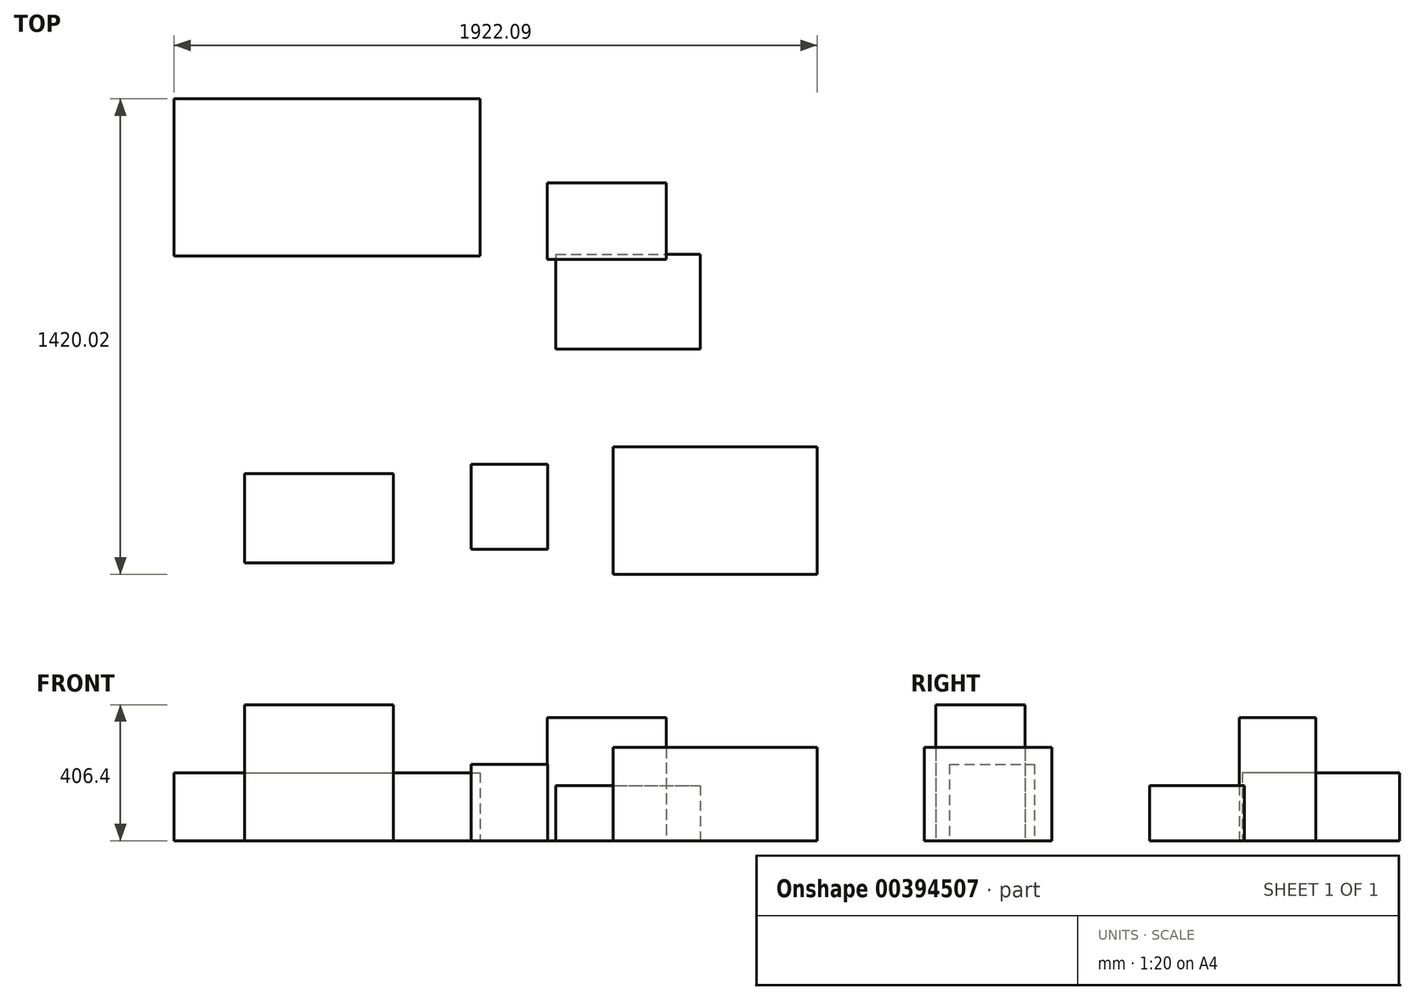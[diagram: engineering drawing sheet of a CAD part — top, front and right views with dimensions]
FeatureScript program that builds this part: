
annotation { "Feature Type Name" : "Feature", "Feature Type Description" : "" }
export const myFeature = defineFeature(function(context is Context, id is Id, definition is map)
    precondition{}
    {
        {
            var Q0;
            Q0=qCreatedBy(makeId("Top.planeOp"),FACE);
            var sketch = newSketch(context, id + "F0", { "sketchPlane" : qUnion([Q0])});
            skLineSegment(sketch, "E0.bottom", {"start": v(-333.22, 250.35) * mm, "end": v(581.18, 250.35) * mm});
            skLineSegment(sketch, "E0.top", {"start": v(-333.22, -219.55) * mm, "end": v(581.18, -219.55) * mm});
            skLineSegment(sketch, "E0.left", {"start": v(-333.22, 250.35) * mm, "end": v(-333.22, -219.55) * mm});
            skLineSegment(sketch, "E0.right", {"start": v(581.18, 250.35) * mm, "end": v(581.18, -219.55) * mm});
            skSolve(sketch);
        }
        {
            var Q0;
            Q0 = qSketchRegion(id + "F0", true);
            extrude(context, id + "F1", {"entities" : qUnion([Q0]), "depth" : 203.2 * mm});
        }
        {
            var Q0;
            Q0=qCreatedBy(makeId("Top.planeOp"),FACE);
            var sketch = newSketch(context, id + "F2", { "sketchPlane" : qUnion([Q0])});
            skLineSegment(sketch, "E1.bottom", {"start": v(782.39, 368.3) * mm, "end": v(1137.99, 368.3) * mm});
            skLineSegment(sketch, "E1.top", {"start": v(782.39, 0) * mm, "end": v(1137.99, 0) * mm});
            skLineSegment(sketch, "E1.left", {"start": v(782.39, 368.3) * mm, "end": v(782.39, 0) * mm});
            skLineSegment(sketch, "E1.right", {"start": v(1137.99, 368.3) * mm, "end": v(1137.99, 0) * mm});
            skSolve(sketch);
        }
        {
            var Q0;
            Q0=makeQuery(id+"F2.imprint","IMPRINT",FACE,{"disambiguationData":[TD([[makeQuery(id+"F2.imprint","IMPRINT",EDGE,{"derivedFrom":sQuery(id+"F2.wireOp",EDGE,"E1.bottom")}),-1.0]])]});
            extrude(context, id + "F3", {"entities" : qUnion([Q0]), "depth" : 228.6 * mm});
        }
        {
            var Q0;
            Q0=qCreatedBy(makeId("Top.planeOp"),FACE);
            var sketch = newSketch(context, id + "F4", { "sketchPlane" : qUnion([Q0])});
            skLineSegment(sketch, "E2.bottom", {"start": v(807.6, -214.07) * mm, "end": v(1239.4, -214.07) * mm});
            skLineSegment(sketch, "E2.top", {"start": v(807.6, -496.64) * mm, "end": v(1239.4, -496.64) * mm});
            skLineSegment(sketch, "E2.left", {"start": v(807.6, -214.07) * mm, "end": v(807.6, -496.64) * mm});
            skLineSegment(sketch, "E2.right", {"start": v(1239.4, -214.07) * mm, "end": v(1239.4, -496.64) * mm});
            skSolve(sketch);
        }
        {
            var Q0;
            Q0=makeQuery(id+"F4.imprint","IMPRINT",FACE,{"disambiguationData":[TD([[makeQuery(id+"F4.imprint","IMPRINT",EDGE,{"derivedFrom":sQuery(id+"F4.wireOp",EDGE,"E2.bottom")}),-1.0]])]});
            extrude(context, id + "F5", {"entities" : qUnion([Q0]), "depth" : 165.1 * mm});
        }
        {
            var Q0;
            Q0=qCreatedBy(makeId("Top.planeOp"),FACE);
            var sketch = newSketch(context, id + "F6", { "sketchPlane" : qUnion([Q0])});
            skLineSegment(sketch, "E3.bottom", {"start": v(-122.07, -462.25) * mm, "end": v(322.43, -462.25) * mm});
            skLineSegment(sketch, "E3.top", {"start": v(-122.07, -868.65) * mm, "end": v(322.43, -868.65) * mm});
            skLineSegment(sketch, "E3.left", {"start": v(-122.07, -462.25) * mm, "end": v(-122.07, -868.65) * mm});
            skLineSegment(sketch, "E3.right", {"start": v(322.43, -462.25) * mm, "end": v(322.43, -868.65) * mm});
            skSolve(sketch);
        }
        {
            var Q0;
            Q0=makeQuery(id+"F6.imprint","IMPRINT",FACE,{"disambiguationData":[TD([[makeQuery(id+"F6.imprint","IMPRINT",EDGE,{"derivedFrom":sQuery(id+"F6.wireOp",EDGE,"E3.bottom")}),-1.0]])]});
            extrude(context, id + "F7", {"entities" : qUnion([Q0]), "depth" : 266.7 * mm});
        }
        {
            var Q0;
            Q0=qCreatedBy(makeId("Top.planeOp"),FACE);
            var sketch = newSketch(context, id + "F8", { "sketchPlane" : qUnion([Q0])});
            skLineSegment(sketch, "E4.bottom", {"start": v(554.05, -613.18) * mm, "end": v(782.65, -613.18) * mm});
            skLineSegment(sketch, "E4.top", {"start": v(554.05, -841.78) * mm, "end": v(782.65, -841.78) * mm});
            skLineSegment(sketch, "E4.left", {"start": v(554.05, -613.18) * mm, "end": v(554.05, -841.78) * mm});
            skLineSegment(sketch, "E4.right", {"start": v(782.65, -613.18) * mm, "end": v(782.65, -841.78) * mm});
            skSolve(sketch);
        }
        {
            var Q0;
            Q0 = qSketchRegion(id + "F8", true);
            extrude(context, id + "F9", {"entities" : qUnion([Q0]), "depth" : 254 * mm});
        }
        {
            var Q0;
            Q0=makeQuery(id+"F3.opExtrude","SWEPT_BODY",BODY,{"disambiguationData":[OSD([sQuery(id+"F2.wireOp",EDGE,"E1.bottom"),sQuery(id+"F2.wireOp",EDGE,"E1.top"),sQuery(id+"F2.wireOp",EDGE,"E1.left"),sQuery(id+"F2.wireOp",EDGE,"E1.right")])]});
            var Q1;
            Q1=makeQuery(id+"F3.opExtrude","CAP_EDGE",EDGE,{"disambiguationData":[OSD([sQuery(id+"F2.wireOp",EDGE,"E1.top")])],"isStart":true});
            transform(context, id + "F10", {"entities" : qUnion([Q0]), "transformType" : TransformType.ROTATION, "transformAxis" : qUnion([Q1]), "angle" : 90 * degree, "makeCopy" : false});
        }
        {
            var Q0;
            Q0=makeQuery(id+"F7.opExtrude","SWEPT_BODY",BODY,{"disambiguationData":[OSD([sQuery(id+"F6.wireOp",EDGE,"E3.bottom"),sQuery(id+"F6.wireOp",EDGE,"E3.top"),sQuery(id+"F6.wireOp",EDGE,"E3.left"),sQuery(id+"F6.wireOp",EDGE,"E3.right")])]});
            var Q1;
            Q1=makeQuery(id+"F7.opExtrude","CAP_EDGE",EDGE,{"disambiguationData":[OSD([sQuery(id+"F6.wireOp",EDGE,"E3.top")])],"isStart":true});
            transform(context, id + "F11", {"entities" : qUnion([Q0]), "transformType" : TransformType.ROTATION, "transformAxis" : qUnion([Q1]), "angle" : 90 * degree, "makeCopy" : false});
        }
        {
            var Q0;
            Q0=makeQuery(id+"F9.opExtrude","SWEPT_BODY",BODY,{"disambiguationData":[OSD([sQuery(id+"F8.wireOp",EDGE,"E4.bottom"),sQuery(id+"F8.wireOp",EDGE,"E4.top"),sQuery(id+"F8.wireOp",EDGE,"E4.left"),sQuery(id+"F8.wireOp",EDGE,"E4.right")])]});
            var Q1;
            Q1=makeQuery(id+"F9.opExtrude","CAP_EDGE",EDGE,{"disambiguationData":[OSD([sQuery(id+"F8.wireOp",EDGE,"E4.top")])],"isStart":true});
            transform(context, id + "F12", {"entities" : qUnion([Q0]), "transformType" : TransformType.ROTATION, "transformAxis" : qUnion([Q1]), "angle" : 90 * degree, "makeCopy" : false});
        }
        {
            var Q0;
            Q0=qCreatedBy(makeId("Top.planeOp"),FACE);
            var sketch = newSketch(context, id + "F13", { "sketchPlane" : qUnion([Q0])});
            skLineSegment(sketch, "E5.bottom", {"start": v(979.27, -788.67) * mm, "end": v(1588.87, -788.67) * mm});
            skLineSegment(sketch, "E5.top", {"start": v(979.27, -1169.67) * mm, "end": v(1588.87, -1169.67) * mm});
            skLineSegment(sketch, "E5.left", {"start": v(979.27, -788.67) * mm, "end": v(979.27, -1169.67) * mm});
            skLineSegment(sketch, "E5.right", {"start": v(1588.87, -788.67) * mm, "end": v(1588.87, -1169.67) * mm});
            skSolve(sketch);
        }
        {
            var Q0;
            Q0 = qSketchRegion(id + "F13", true);
            extrude(context, id + "F14", {"entities" : qUnion([Q0]), "depth" : 279.4 * mm});
        }
    });
